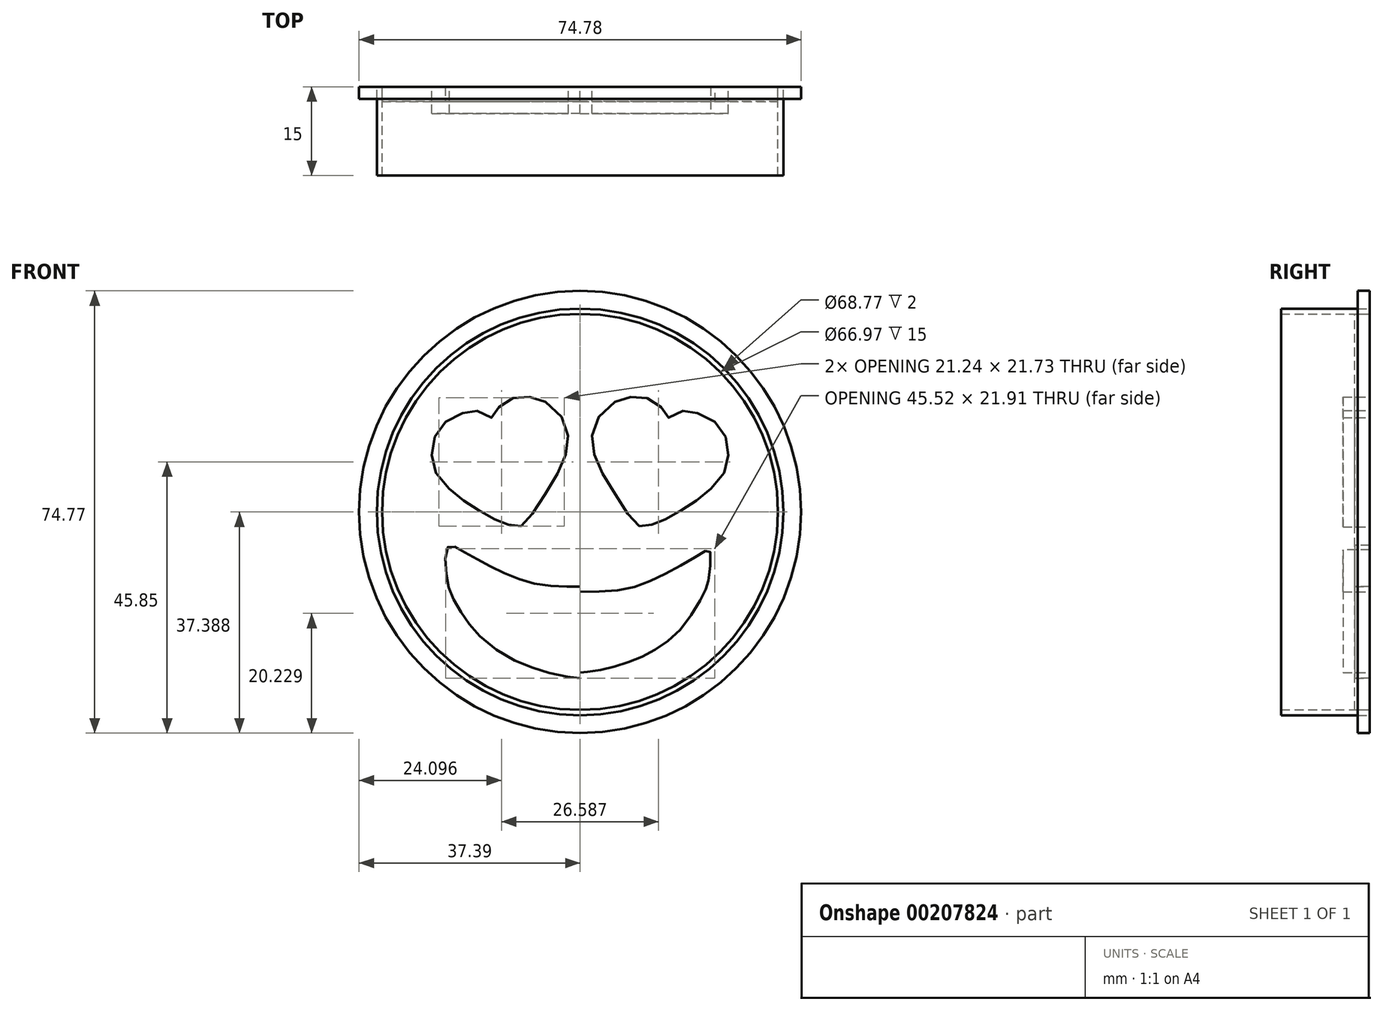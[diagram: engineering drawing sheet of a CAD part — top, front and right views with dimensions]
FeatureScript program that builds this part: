
annotation { "Feature Type Name" : "Feature", "Feature Type Description" : "" }
export const myFeature = defineFeature(function(context is Context, id is Id, definition is map)
    precondition{}
    {
        {
            var Q0;
            Q0=qCreatedBy(makeId("Front.planeOp"),FACE);
            var sketch = newSketch(context, id + "F0", { "sketchPlane" : qUnion([Q0])});
            skCircle(sketch, "E0", {"center": v(0, 4.62) * mm, "radius": 33.49 * mm});
            skFitSpline(sketch, "E1", {"points": [v(-10, 2.21) * mm, v(-7.5, 5.21) * mm, v(-3.77, 11.2) * mm, v(-2.08, 15.85) * mm, v(-2.9, 20.34) * mm, v(-7, 23.77) * mm, v(-9.86, 23.97) * mm, v(-13.34, 23) * mm, v(-14.7, 20.58) * mm, v(-17.16, 21.6) * mm, v(-19.72, 21.4) * mm, v(-23.54, 19.18) * mm, v(-25.04, 15.22) * mm, v(-24.4, 11.3) * mm, v(-21.03, 7.58) * mm, v(-18.08, 5.45) * mm, v(-14.3, 3.28) * mm, v(-11.99, 2.4) * mm, v(-10, 2.21) * mm]});
            skFitSpline(sketch, "E2", {"points": [v(0, -8.9) * mm, v(-8.67, -8.2) * mm, v(-15.34, -5.33) * mm, v(-20.86, -2.22) * mm, v(-21.9, -1.88) * mm, v(-21.78, -6.6) * mm, v(-21.09, -8.9) * mm, v(-17.3, -14.87) * mm, v(-12.12, -19) * mm, v(-7.06, -21.2) * mm, v(-2, -22.34) * mm, v(0, -22.57) * mm, v(0, -22.64) * mm], "startDerivative": vector(-75.28, 0.62) * mm, "endDerivative": vector(-2.48, -6.38) * mm});
            skFitSpline(sketch, "E3.MirrorC", {"points": [v(10, 2.21) * mm, v(7.5, 5.21) * mm, v(3.77, 11.2) * mm, v(2.08, 15.85) * mm, v(2.9, 20.34) * mm, v(7, 23.77) * mm, v(9.86, 23.97) * mm, v(13.34, 23) * mm, v(14.7, 20.58) * mm, v(17.16, 21.6) * mm, v(19.72, 21.4) * mm, v(23.54, 19.18) * mm, v(25.04, 15.22) * mm, v(24.4, 11.3) * mm, v(21.03, 7.58) * mm, v(18.08, 5.45) * mm, v(14.3, 3.28) * mm, v(11.99, 2.4) * mm, v(10, 2.21) * mm]});
            skFitSpline(sketch, "E4.MirrorCS", {"points": [v(0, -8.9) * mm, v(8.67, -8.2) * mm, v(15.34, -5.33) * mm, v(20.86, -2.22) * mm, v(21.9, -1.88) * mm, v(21.78, -6.6) * mm, v(21.09, -8.9) * mm, v(17.3, -14.87) * mm, v(12.12, -19) * mm, v(7.06, -21.2) * mm, v(2, -22.34) * mm, v(0, -22.57) * mm, v(0, -22.64) * mm], "startDerivative": vector(75.28, 0.62) * mm, "endDerivative": vector(2.48, -6.38) * mm});
            skPoint(sketch, "E5.orphan", {"position": v(0, 32.83) * mm});
            skCircle(sketch, "E6.0", {"center": v(0, 4.62) * mm, "radius": 34.39 * mm});
            skFitSpline(sketch, "E7.0", {"points": [v(-10.33, 2.74) * mm, v(-10.22, 2.77) * mm, v(-10.11, 2.82) * mm, v(-9.95, 2.92) * mm, v(-9.72, 3.11) * mm, v(-9.42, 3.43) * mm, v(-9, 3.97) * mm, v(-8.55, 4.65) * mm, v(-8.07, 5.41) * mm, v(-7.57, 6.2) * mm, v(-6.9, 7.23) * mm, v(-6.1, 8.5) * mm, v(-5.3, 9.75) * mm, v(-4.57, 10.99) * mm, v(-3.93, 12.16) * mm, v(-3.4, 13.27) * mm, v(-3, 14.35) * mm, v(-2.74, 15.41) * mm, v(-2.59, 16.5) * mm, v(-2.6, 17.57) * mm, v(-2.77, 18.64) * mm, v(-3.1, 19.5) * mm, v(-3.48, 20.16) * mm, v(-3.96, 20.82) * mm, v(-4.7, 21.61) * mm, v(-5.53, 22.29) * mm, v(-6.2, 22.72) * mm, v(-6.7, 23) * mm, v(-7.15, 23.2) * mm, v(-7.57, 23.33) * mm, v(-7.95, 23.4) * mm, v(-8.34, 23.43) * mm, v(-8.74, 23.43) * mm, v(-9.17, 23.41) * mm, v(-9.66, 23.38) * mm, v(-10.2, 23.35) * mm, v(-10.73, 23.31) * mm, v(-11.26, 23.26) * mm, v(-11.76, 23.18) * mm, v(-12.2, 23.05) * mm, v(-12.51, 22.9) * mm, v(-12.71, 22.77) * mm, v(-12.84, 22.66) * mm, v(-12.95, 22.53) * mm, v(-13.06, 22.37) * mm, v(-13.17, 22.18) * mm, v(-13.3, 21.9) * mm, v(-13.45, 21.5) * mm, v(-13.6, 21.1) * mm, v(-13.74, 20.78) * mm, v(-13.87, 20.55) * mm, v(-14.04, 20.32) * mm, v(-14.24, 20.14) * mm, v(-14.44, 20.03) * mm, v(-14.67, 19.96) * mm, v(-14.94, 19.93) * mm, v(-15.23, 19.98) * mm, v(-15.5, 20.06) * mm, v(-15.74, 20.16) * mm, v(-16.06, 20.32) * mm, v(-16.45, 20.55) * mm, v(-16.9, 20.81) * mm, v(-17.24, 20.99) * mm, v(-17.48, 21.08) * mm, v(-17.7, 21.14) * mm, v(-17.96, 21.18) * mm, v(-18.29, 21.17) * mm, v(-18.64, 21.11) * mm, v(-19.04, 21) * mm, v(-19.49, 20.85) * mm, v(-19.98, 20.67) * mm, v(-20.65, 20.4) * mm, v(-21.51, 20) * mm, v(-22.3, 19.5) * mm, v(-22.85, 19.04) * mm, v(-23.2, 18.67) * mm, v(-23.5, 18.27) * mm, v(-23.83, 17.68) * mm, v(-24.15, 16.86) * mm, v(-24.38, 15.8) * mm, v(-24.5, 14.72) * mm, v(-24.5, 13.7) * mm, v(-24.34, 12.72) * mm, v(-24.07, 11.94) * mm, v(-23.74, 11.32) * mm, v(-23.33, 10.7) * mm, v(-22.7, 9.93) * mm, v(-21.81, 9.05) * mm, v(-21.05, 8.38) * mm, v(-20.47, 7.9) * mm, v(-19.92, 7.46) * mm, v(-19.25, 6.96) * mm, v(-18.58, 6.5) * mm, v(-18, 6.12) * mm, v(-17.4, 5.72) * mm, v(-16.56, 5.2) * mm, v(-15.54, 4.6) * mm, v(-14.72, 4.15) * mm, v(-14.1, 3.84) * mm, v(-13.54, 3.59) * mm, v(-13.02, 3.38) * mm, v(-12.52, 3.2) * mm, v(-12.2, 3.1) * mm, v(-11.95, 3.02) * mm, v(-11.69, 2.94) * mm, v(-11.37, 2.84) * mm, v(-11.02, 2.75) * mm, v(-10.7, 2.7) * mm, v(-10.49, 2.7) * mm, v(-10.33, 2.74) * mm, v(-10.22, 2.77) * mm, v(-10.11, 2.82) * mm, v(-10.33, 2.74) * mm]});
            skFitSpline(sketch, "E8.0", {"points": [v(10.33, 2.74) * mm, v(10.22, 2.77) * mm, v(10.11, 2.82) * mm, v(9.95, 2.92) * mm, v(9.72, 3.11) * mm, v(9.42, 3.43) * mm, v(9, 3.97) * mm, v(8.55, 4.65) * mm, v(8.07, 5.41) * mm, v(7.57, 6.2) * mm, v(6.9, 7.23) * mm, v(6.1, 8.5) * mm, v(5.3, 9.75) * mm, v(4.57, 10.99) * mm, v(3.93, 12.16) * mm, v(3.4, 13.27) * mm, v(3, 14.35) * mm, v(2.74, 15.41) * mm, v(2.59, 16.5) * mm, v(2.6, 17.57) * mm, v(2.77, 18.64) * mm, v(3.1, 19.5) * mm, v(3.48, 20.16) * mm, v(3.96, 20.82) * mm, v(4.7, 21.61) * mm, v(5.53, 22.29) * mm, v(6.2, 22.72) * mm, v(6.7, 23) * mm, v(7.15, 23.2) * mm, v(7.57, 23.33) * mm, v(7.95, 23.4) * mm, v(8.34, 23.43) * mm, v(8.74, 23.43) * mm, v(9.17, 23.41) * mm, v(9.66, 23.38) * mm, v(10.2, 23.35) * mm, v(10.73, 23.31) * mm, v(11.26, 23.26) * mm, v(11.76, 23.18) * mm, v(12.2, 23.05) * mm, v(12.51, 22.9) * mm, v(12.71, 22.77) * mm, v(12.84, 22.66) * mm, v(12.95, 22.53) * mm, v(13.06, 22.37) * mm, v(13.17, 22.18) * mm, v(13.3, 21.9) * mm, v(13.45, 21.5) * mm, v(13.6, 21.1) * mm, v(13.74, 20.78) * mm, v(13.87, 20.55) * mm, v(14.04, 20.32) * mm, v(14.24, 20.14) * mm, v(14.44, 20.03) * mm, v(14.67, 19.96) * mm, v(14.94, 19.93) * mm, v(15.23, 19.98) * mm, v(15.5, 20.06) * mm, v(15.74, 20.16) * mm, v(16.06, 20.32) * mm, v(16.45, 20.55) * mm, v(16.9, 20.81) * mm, v(17.24, 20.99) * mm, v(17.48, 21.08) * mm, v(17.7, 21.14) * mm, v(17.96, 21.18) * mm, v(18.29, 21.17) * mm, v(18.64, 21.11) * mm, v(19.04, 21) * mm, v(19.49, 20.85) * mm, v(19.98, 20.67) * mm, v(20.65, 20.4) * mm, v(21.51, 20) * mm, v(22.3, 19.5) * mm, v(22.85, 19.04) * mm, v(23.2, 18.67) * mm, v(23.5, 18.27) * mm, v(23.83, 17.68) * mm, v(24.15, 16.86) * mm, v(24.38, 15.8) * mm, v(24.5, 14.72) * mm, v(24.5, 13.7) * mm, v(24.34, 12.72) * mm, v(24.07, 11.94) * mm, v(23.74, 11.32) * mm, v(23.33, 10.7) * mm, v(22.7, 9.93) * mm, v(21.81, 9.05) * mm, v(21.05, 8.38) * mm, v(20.47, 7.9) * mm, v(19.92, 7.46) * mm, v(19.25, 6.96) * mm, v(18.58, 6.5) * mm, v(18, 6.12) * mm, v(17.4, 5.72) * mm, v(16.56, 5.2) * mm, v(15.54, 4.6) * mm, v(14.72, 4.15) * mm, v(14.1, 3.84) * mm, v(13.54, 3.59) * mm, v(13.02, 3.38) * mm, v(12.52, 3.2) * mm, v(12.2, 3.1) * mm, v(11.95, 3.02) * mm, v(11.69, 2.94) * mm, v(11.37, 2.84) * mm, v(11.02, 2.75) * mm, v(10.7, 2.7) * mm, v(10.49, 2.7) * mm, v(10.33, 2.74) * mm, v(10.22, 2.77) * mm, v(10.11, 2.82) * mm, v(10.33, 2.74) * mm]});
            skLineSegment(sketch, "E9", {"start": v(0, -8) * mm, "end": v(0, -8) * mm});
            skFitSpline(sketch, "E10", {"points": [v(0, -8) * mm, v(2.66, -8) * mm, v(6.71, -7.69) * mm, v(10.3, -6.74) * mm, v(13.87, -5.27) * mm, v(16.77, -3.66) * mm, v(19.47, -2.26) * mm, v(21.14, -1.28) * mm, v(22.03, -1.08) * mm, v(22.72, -2.08) * mm, v(22.7, -5.27) * mm, v(22.26, -7.99) * mm, v(21.28, -10.36) * mm, v(19.59, -13.2) * mm, v(17.6, -15.74) * mm, v(12.65, -19.67) * mm, v(7.35, -21.97) * mm, v(2.92, -23.12) * mm, v(0, -23.5) * mm, v(0, -23.5) * mm], "startDerivative": vector(48.98, -0.57) * mm, "endDerivative": vector(0.64, 1.3) * mm});
            skFitSpline(sketch, "E11.MirrorCS", {"points": [v(0, -8) * mm, v(-2.66, -8) * mm, v(-6.71, -7.69) * mm, v(-10.3, -6.74) * mm, v(-13.87, -5.27) * mm, v(-16.77, -3.66) * mm, v(-19.47, -2.26) * mm, v(-21.14, -1.28) * mm, v(-22.03, -1.08) * mm, v(-22.72, -2.08) * mm, v(-22.7, -5.27) * mm, v(-22.26, -7.99) * mm, v(-21.28, -10.36) * mm, v(-19.59, -13.2) * mm, v(-17.6, -15.74) * mm, v(-12.65, -19.67) * mm, v(-7.35, -21.97) * mm, v(-2.92, -23.12) * mm, v(0, -23.5) * mm, v(0, -23.5) * mm], "startDerivative": vector(-48.98, -0.57) * mm, "endDerivative": vector(-0.64, 1.3) * mm});
            skSolve(sketch);
        }
        {
            var Q0;
            Q0=makeQuery(id+"F0.imprint","IMPRINT",FACE,{"disambiguationData":[TD([[makeQuery(id+"F0.imprint","IMPRINT",EDGE,{"derivedFrom":sQuery(id+"F0.wireOp",EDGE,"E1")}),1.0]])]});
            var Q1;
            Q1=makeQuery(id+"F0.imprint","IMPRINT",FACE,{"disambiguationData":[TD([[makeQuery(id+"F0.imprint","IMPRINT",EDGE,{"derivedFrom":sQuery(id+"F0.wireOp",EDGE,"E3.MirrorC")}),-1.0]])]});
            var Q2;
            Q2=makeQuery(id+"F0.imprint","IMPRINT",FACE,{"disambiguationData":[TD([[makeQuery(id+"F0.imprint","IMPRINT",EDGE,{"derivedFrom":sQuery(id+"F0.wireOp",EDGE,"E2")}),1.0]])]});
            extrude(context, id + "F1", {"entities" : qUnion([Q0, Q1, Q2]), "depth" : 4.5 * mm});
        }
        {
            var Q0;
            Q0=makeQuery(id+"F0.imprint","IMPRINT",FACE,{"disambiguationData":[TD([[makeQuery(id+"F0.imprint","IMPRINT",EDGE,{"derivedFrom":sQuery(id+"F0.wireOp",EDGE,"E0")}),1.0]])]});
            var Q1;
            Q1=makeQuery(id+"F0.imprint","IMPRINT",FACE,{"disambiguationData":[TD([[makeQuery(id+"F0.imprint","IMPRINT",EDGE,{"derivedFrom":sQuery(id+"F0.wireOp",EDGE,"E7.0")}),1.0]])]});
            var Q2;
            Q2=makeQuery(id+"F0.imprint","IMPRINT",FACE,{"disambiguationData":[TD([[makeQuery(id+"F0.imprint","IMPRINT",EDGE,{"derivedFrom":sQuery(id+"F0.wireOp",EDGE,"E8.0")}),-1.0]])]});
            var Q3;
            Q3=makeQuery(id+"F0.imprint","IMPRINT",FACE,{"disambiguationData":[TD([[makeQuery(id+"F0.imprint","IMPRINT",EDGE,{"derivedFrom":sQuery(id+"F0.wireOp",EDGE,"E2")}),1.0]])]});
            extrude(context, id + "F2", {"entities" : qUnion([Q0, Q1, Q2, Q3]), "depth" : 2.5 * mm});
        }
        {
            var Q0;
            Q0=qCreatedBy(makeId("Front.planeOp"),FACE);
            var sketch = newSketch(context, id + "F3", { "sketchPlane" : qUnion([Q0])});
            skCircle(sketch, "E12.0", {"center": v(0, 4.62) * mm, "radius": 34.39 * mm});
            skCircle(sketch, "E12.1", {"center": v(0, 4.62) * mm, "radius": 33.49 * mm});
            skCircle(sketch, "E13.0", {"center": v(0, 4.62) * mm, "radius": 37.39 * mm});
            skSolve(sketch);
        }
        {
            var Q0;
            Q0=makeQuery(id+"F3.imprint","IMPRINT",FACE,{"disambiguationData":[TD([[makeQuery(id+"F3.imprint","IMPRINT",EDGE,{"derivedFrom":sQuery(id+"F3.wireOp",EDGE,"E12.1")}),1.0]])]});
            extrude(context, id + "F4", {"entities" : qUnion([Q0]), "depth" : 2.5 * mm});
        }
        {
            var Q0;
            Q0 = qSketchRegion(id + "F3", true);
            extrude(context, id + "F5", {"entities" : qUnion([Q0]), "depth" : 2 * mm});
        }
        {
            var Q0;
            Q0=makeQuery(id+"F3.imprint","IMPRINT",FACE,{"disambiguationData":[TD([[makeQuery(id+"F3.imprint","IMPRINT",EDGE,{"derivedFrom":sQuery(id+"F3.wireOp",EDGE,"E12.0")}),1.0]])]});
            extrude(context, id + "F6", {"entities" : qUnion([Q0]), "depth" : 15 * mm});
        }
    });
